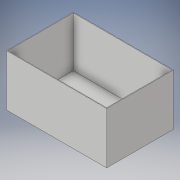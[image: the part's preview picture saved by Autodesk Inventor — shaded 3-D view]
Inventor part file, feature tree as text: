
AUTODESK INVENTOR PART (.ipt)
format: ipt  version: 2018 (Build 220112000, 112)  size: 113,664 bytes
history: native  units: in
note: dims shown in document units (in); Inventor stores cm internally (conversion verified against a paired STEP export)
features: extrude x3, sketch x3
ambient origin geometry x8: Origin, YZ Plane, XZ Plane, XY Plane, X Axis, Y Axis, Z Axis, Center Point
bodies: Solid1 (feature_tree)
feature tree (6):
  extrude  "Extrusion1"  Depth=4.0in
  extrude  "Extrusion2"  Depth=5.92in
  extrude  "Extrusion3"  Depth=3.0in TaperAngle=0.0deg
  sketch  "Sketch1"  dims[d0=6.0in d1=4.0in]
  sketch  "Sketch2"  dims[d2=0.08in d3=0.0in d4=5.92in]
  sketch  "Sketch3"  dims[d5=3.92in d6=3.0in d7=0.0in d10=0.164in d11=0.164in d12=0.0in d13=0.0in]
